# Revit family: xFlush_Valve-AC_Toilet-American_Standard-Exposed-Top_Spud-606B_Series
name_source: partatom
category: Plumbing Fixtures
revit_build: Autodesk Revit 2014 (Build: 20130308_1515(x64)
units: mm (PartAtom-declared; Revit-internal decimal feet)

## types (6) — shared parameters
ADA Compliant = Yes
Assembly Code = D2020100
CW Connection = Yes
CWFU = 10
Cold Water Connection Diameter = 1"
Cold Water Connection Height = 11 1/2"
Cold Water Connection Radius = 1/2"
Cold Water Connection Width = 4 1/2"
Default Elevation = 0"
Description = Selectronic Exposed AC Toilet Flush Valve
Electrical Box & Cover Height = 23 3/8"
Electrical Box & Cover Width = 8 1/2"
HW Connection = No
Height = 16 1/8"
Installation Type = Exposed
Length = 2 1/4"
Manufacturer = American Standard
Material = Metal-American Standard-002-Polished Chrome
PK00.BBU - Battery Back-Up = No
PK00.HAC - Hard Wired AC - Power Kit = No
PK00.MAC - Multi-AC - Power Kit = No
Price = Prices may vary. Please consult Manufacturer Representative for most up-to-date price list.
Product Page URL = https://www.americanstandard-us.com
Revised Date = 12/23/2016
URL = http://www.americanstandard-us.com
Vent Connection = No
Warranty Information = 1 Year Limited Warranty
Waste Connection = No
Width = 2 7/8"
zero-valued in all types: HWFU, WFU

## per-type parameters (varying)
| type | Flush Rate |
| 606B.161 | 1.6 gpf /6.0 Lpf |
| 606B.121 | 1.28 gpf/4.8 Lpf |
| 606B.111 | 1.1 gpf/4.2 Lpf |
| 606B.XXX | 1.0 gpf/3.8 Lpf |
| 606B.761 | 1.6 gpf/1.1 gpf (6.0/4.2 Lpf) |
| 606B.721 | 1.28 gpf/1.1 gpf (4.8/4.2 Lpf) |

note: column(s) folded — value = type name in every type: Model

## geometry (parser evidence)
native form markers: Sweep x1
no freeform markers — native parametric forms only
